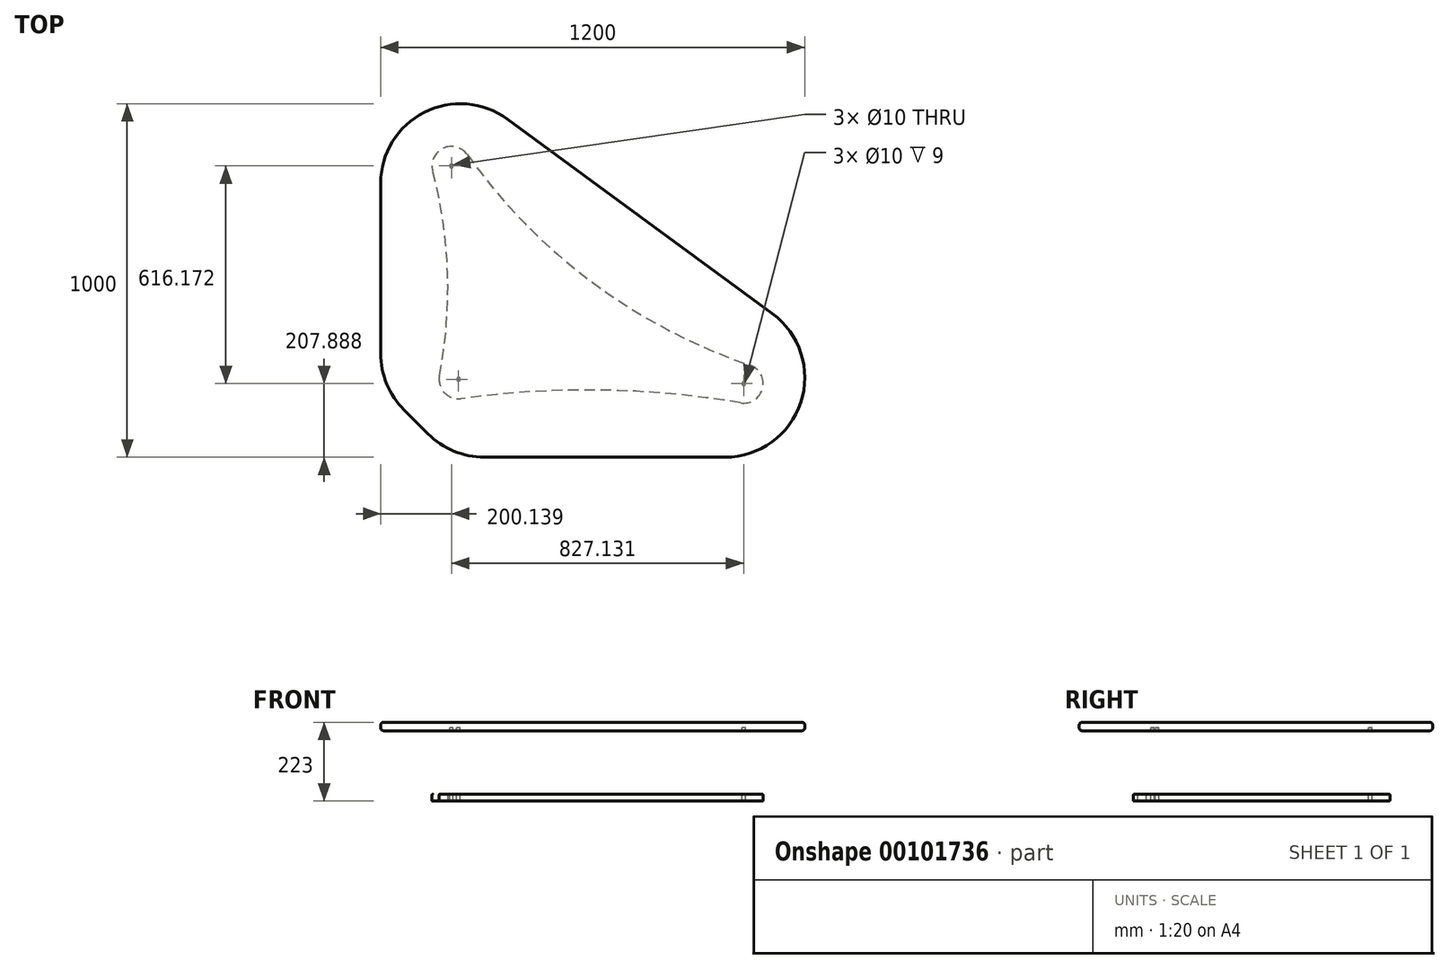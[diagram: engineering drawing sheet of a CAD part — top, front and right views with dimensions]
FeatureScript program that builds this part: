
annotation { "Feature Type Name" : "Feature", "Feature Type Description" : "" }
export const myFeature = defineFeature(function(context is Context, id is Id, definition is map)
    precondition{}
    {
        {
            var Q0;
            Q0=qCreatedBy(makeId("Top.planeOp"),FACE);
            var sketch = newSketch(context, id + "F0", { "sketchPlane" : qUnion([Q0])});
            skLineSegment(sketch, "E0", {"start": v(0, 775) * mm, "end": v(0, 293.2) * mm});
            skLineSegment(sketch, "E1", {"start": v(293.2, 0) * mm, "end": v(975, 0) * mm});
            skLineSegment(sketch, "E2", {"start": v(1108.06, 406.44) * mm, "end": v(358.06, 956.44) * mm});
            skLineSegment(sketch, "E3", {"start": v(65.9, 134.1) * mm, "end": v(134.1, 65.9) * mm});
            skPoint(sketch, "E4.visualSharp", {"position": v(0, 200) * mm});
            skArc(sketch, "E4.filletArc", {"start": v(0, 293.2) * mm, "mid": v(17.13, 207.1) * mm, "end": v(65.9, 134.1) * mm});
            skPoint(sketch, "E5.visualSharp", {"position": v(200, 0) * mm});
            skArc(sketch, "E5.filletArc", {"start": v(134.1, 65.9) * mm, "mid": v(207.1, 17.13) * mm, "end": v(293.2, 0) * mm});
            skPoint(sketch, "E6.visualSharp", {"position": v(1662.3, 0) * mm});
            skArc(sketch, "E6.filletArc", {"start": v(975, 0) * mm, "mid": v(1188.83, 155) * mm, "end": v(1108.06, 406.44) * mm});
            skPoint(sketch, "E7.visualSharp", {"position": v(0, 1219.02) * mm});
            skArc(sketch, "E7.filletArc", {"start": v(358.06, 956.44) * mm, "mid": v(123.3, 975.7) * mm, "end": v(0, 775) * mm});
            skArc(sketch, "E8.0", {"start": v(244.93, 855.98) * mm, "mid": v(176.78, 873.85) * mm, "end": v(146.96, 810.03) * mm});
            skArc(sketch, "E8.3", {"start": v(1018.14, 153.65) * mm, "mid": v(1080.59, 194.4) * mm, "end": v(1045.04, 259.94) * mm});
            skArc(sketch, "E8.4", {"start": v(166.21, 230.68) * mm, "mid": v(180.26, 182.4) * mm, "end": v(227.68, 165.72) * mm});
            skLineSegment(sketch, "E9", {"start": v(-750, 1188.7) * mm, "end": v(-200, 1188.7) * mm, "construction": true});
            skLineSegment(sketch, "E10", {"start": v(-200, 1188.7) * mm, "end": v(-200, 68.7) * mm, "construction": true});
            skLineSegment(sketch, "E11", {"start": v(-200, 68.7) * mm, "end": v(68.7, -200) * mm, "construction": true});
            skLineSegment(sketch, "E12", {"start": v(68.7, -200) * mm, "end": v(2028.7, -200) * mm, "construction": true});
            skLineSegment(sketch, "E13", {"start": v(2028.7, -200) * mm, "end": v(2028.7, -750) * mm, "construction": true});
            skLineSegment(sketch, "E14", {"start": v(2028.7, -750) * mm, "end": v(68.7, -750) * mm, "construction": true});
            skLineSegment(sketch, "E15.bottom", {"start": v(1148.7, 600) * mm, "end": v(1748.7, 600) * mm, "construction": true});
            skLineSegment(sketch, "E15.top", {"start": v(1148.7, 0) * mm, "end": v(1748.7, 0) * mm, "construction": true});
            skLineSegment(sketch, "E15.left", {"start": v(1148.7, 600) * mm, "end": v(1148.7, 0) * mm, "construction": true});
            skLineSegment(sketch, "E15.right", {"start": v(1748.7, 600) * mm, "end": v(1748.7, 0) * mm, "construction": true});
            skLineSegment(sketch, "E16", {"start": v(1748.7, -200) * mm, "end": v(1748.7, -750) * mm, "construction": true});
            skLineSegment(sketch, "E17", {"start": v(908.7, -200) * mm, "end": v(908.7, -750) * mm, "construction": true});
            skLineSegment(sketch, "E18", {"start": v(68.7, -200) * mm, "end": v(68.7, -750) * mm, "construction": true});
            skLineSegment(sketch, "E19", {"start": v(68.7, -750) * mm, "end": v(-578.22, -578.22) * mm, "construction": true});
            skLineSegment(sketch, "E20", {"start": v(-578.22, -578.22) * mm, "end": v(-750, 68.7) * mm, "construction": true});
            skLineSegment(sketch, "E21", {"start": v(-200, 68.7) * mm, "end": v(-750, 68.7) * mm, "construction": true});
            skLineSegment(sketch, "E22", {"start": v(-750, 1188.7) * mm, "end": v(-750, 68.7) * mm, "construction": true});
            skLineSegment(sketch, "E23", {"start": v(-750, 908.7) * mm, "end": v(-200, 908.7) * mm, "construction": true});
            skCircle(sketch, "E24", {"center": v(200.14, 824.06) * mm, "radius": 27.5 * mm, "construction": true});
            skArc(sketch, "E25", {"start": v(244.93, 855.98) * mm, "mid": v(598.2, 495.17) * mm, "end": v(1045.04, 259.94) * mm});
            skArc(sketch, "E26", {"start": v(166.21, 230.68) * mm, "mid": v(189.28, 521.44) * mm, "end": v(146.96, 810.03) * mm});
            skArc(sketch, "E27", {"start": v(1018.14, 153.65) * mm, "mid": v(623.37, 189.7) * mm, "end": v(227.68, 165.72) * mm});
            skCircle(sketch, "E28", {"center": v(220.2, 220.2) * mm, "radius": 27.5 * mm, "construction": true});
            skCircle(sketch, "E29", {"center": v(1027.27, 207.89) * mm, "radius": 27.5 * mm, "construction": true});
            skLineSegment(sketch, "E30", {"start": v(225, 775) * mm, "end": v(276.2, 673.96) * mm, "construction": true});
            skLineSegment(sketch, "E31", {"start": v(975, 225) * mm, "end": v(916.12, 244.28) * mm, "construction": true});
            skLineSegment(sketch, "E32", {"start": v(0, 0) * mm, "end": v(220.2, 220.2) * mm, "construction": true});
            skCircle(sketch, "E33", {"center": v(220.2, 220.2) * mm, "radius": 5 * mm});
            skCircle(sketch, "E34", {"center": v(200.14, 824.06) * mm, "radius": 5 * mm});
            skCircle(sketch, "E35", {"center": v(1027.27, 207.89) * mm, "radius": 5 * mm});
            skSolve(sketch);
        }
        {
            var Q0;
            Q0=makeQuery(id+"F0.imprint","IMPRINT",FACE,{"disambiguationData":[TD([[makeQuery(id+"F0.imprint","IMPRINT",EDGE,{"derivedFrom":sQuery(id+"F0.wireOp",EDGE,"E0")}),1.0]])]});
            var Q1;
            Q1=makeQuery(id+"F0.imprint","IMPRINT",FACE,{"disambiguationData":[TD([[makeQuery(id+"F0.imprint","IMPRINT",EDGE,{"derivedFrom":sQuery(id+"F0.wireOp",EDGE,"E8.0")}),1.0]])]});
            var Q2;
            Q2=makeQuery(id+"F0.imprint","IMPRINT",FACE,{"disambiguationData":[TD([[makeQuery(id+"F0.imprint","IMPRINT",EDGE,{"derivedFrom":sQuery(id+"F0.wireOp",EDGE,"E33")}),1.0]])]});
            var Q3;
            Q3=makeQuery(id+"F0.imprint","IMPRINT",FACE,{"disambiguationData":[TD([[makeQuery(id+"F0.imprint","IMPRINT",EDGE,{"derivedFrom":sQuery(id+"F0.wireOp",EDGE,"E34")}),1.0]])]});
            var Q4;
            Q4=makeQuery(id+"F0.imprint","IMPRINT",FACE,{"disambiguationData":[TD([[makeQuery(id+"F0.imprint","IMPRINT",EDGE,{"derivedFrom":sQuery(id+"F0.wireOp",EDGE,"E35")}),1.0]])]});
            extrude(context, id + "F1", {"entities" : qUnion([Q0, Q1, Q2, Q3, Q4]), "oppositeDirection" : true, "depth" : 24 * mm});
        }
        {
            var Q0;
            Q0=makeQuery(id+"F0.imprint","IMPRINT",FACE,{"disambiguationData":[TD([[makeQuery(id+"F0.imprint","IMPRINT",EDGE,{"derivedFrom":sQuery(id+"F0.wireOp",EDGE,"E35")}),1.0]])]});
            var Q1;
            Q1=makeQuery(id+"F0.imprint","IMPRINT",FACE,{"disambiguationData":[TD([[makeQuery(id+"F0.imprint","IMPRINT",EDGE,{"derivedFrom":sQuery(id+"F0.wireOp",EDGE,"E33")}),1.0]])]});
            var Q2;
            Q2=makeQuery(id+"F0.imprint","IMPRINT",FACE,{"disambiguationData":[TD([[makeQuery(id+"F0.imprint","IMPRINT",EDGE,{"derivedFrom":sQuery(id+"F0.wireOp",EDGE,"E34")}),1.0]])]});
            extrude(context, id + "F2", {"entities" : qUnion([Q0, Q1, Q2]), "operationType" : NewBodyOperationType.REMOVE, "endBound" : BoundingType.THROUGH_ALL, "oppositeDirection" : true, "depth" : 20 * mm, "hasSecondDirection" : true, "secondDirectionOppositeDirection" : true, "secondDirectionDepth" : 15 * mm});
        }
        {
            var Q0;
            Q0=makeQuery(id+"F1.opExtrude","CAP_EDGE",EDGE,{"disambiguationData":[OSD([sQuery(id+"F0.wireOp",EDGE,"E3")])],"isStart":true});
            var Q1;
            Q1=makeQuery(id+"F1.opExtrude","CAP_EDGE",EDGE,{"disambiguationData":[OSD([sQuery(id+"F0.wireOp",EDGE,"E8.5")])],"isStart":true});
            var Q2;
            Q2=makeQuery(id+"F1.opExtrude","CAP_EDGE",EDGE,{"disambiguationData":[OSD([sQuery(id+"F0.wireOp",EDGE,"E8.2")])],"isStart":false});
            var Q3;
            Q3=makeQuery(id+"F1.opExtrude","CAP_EDGE",EDGE,{"disambiguationData":[OSD([sQuery(id+"F0.wireOp",EDGE,"E1")])],"isStart":false});
            fillet(context, id + "F3", {"entities" : qUnion([Q0, Q1, Q2, Q3]), "radius" : 8 * mm, "tangentPropagation" : true, "allowEdgeOverflow" : false});
        }
        {
            var Q0;
            Q0=makeQuery(id+"F0.imprint","IMPRINT",FACE,{"disambiguationData":[TD([[makeQuery(id+"F0.imprint","IMPRINT",EDGE,{"derivedFrom":sQuery(id+"F0.wireOp",EDGE,"E8.0")}),1.0]])]});
            extrude(context, id + "F4", {"entities" : qUnion([Q0]), "oppositeDirection" : true, "depth" : 223 * mm, "hasSecondDirection" : true, "secondDirectionOppositeDirection" : true, "secondDirectionDepth" : 204 * mm});
        }
        {
            var Q0;
            Q0=makeQuery(id+"F4.opExtrude","CAP_EDGE",EDGE,{"disambiguationData":[OSD([sQuery(id+"F0.wireOp",EDGE,"E27")])],"isStart":true});
            var Q1;
            Q1=makeQuery(id+"F4.opExtrude","CAP_EDGE",EDGE,{"disambiguationData":[OSD([sQuery(id+"F0.wireOp",EDGE,"E27")])],"isStart":false});
            fillet(context, id + "F5", {"entities" : qUnion([Q0, Q1]), "radius" : 2 * mm, "tangentPropagation" : true, "allowEdgeOverflow" : false});
        }
    });
